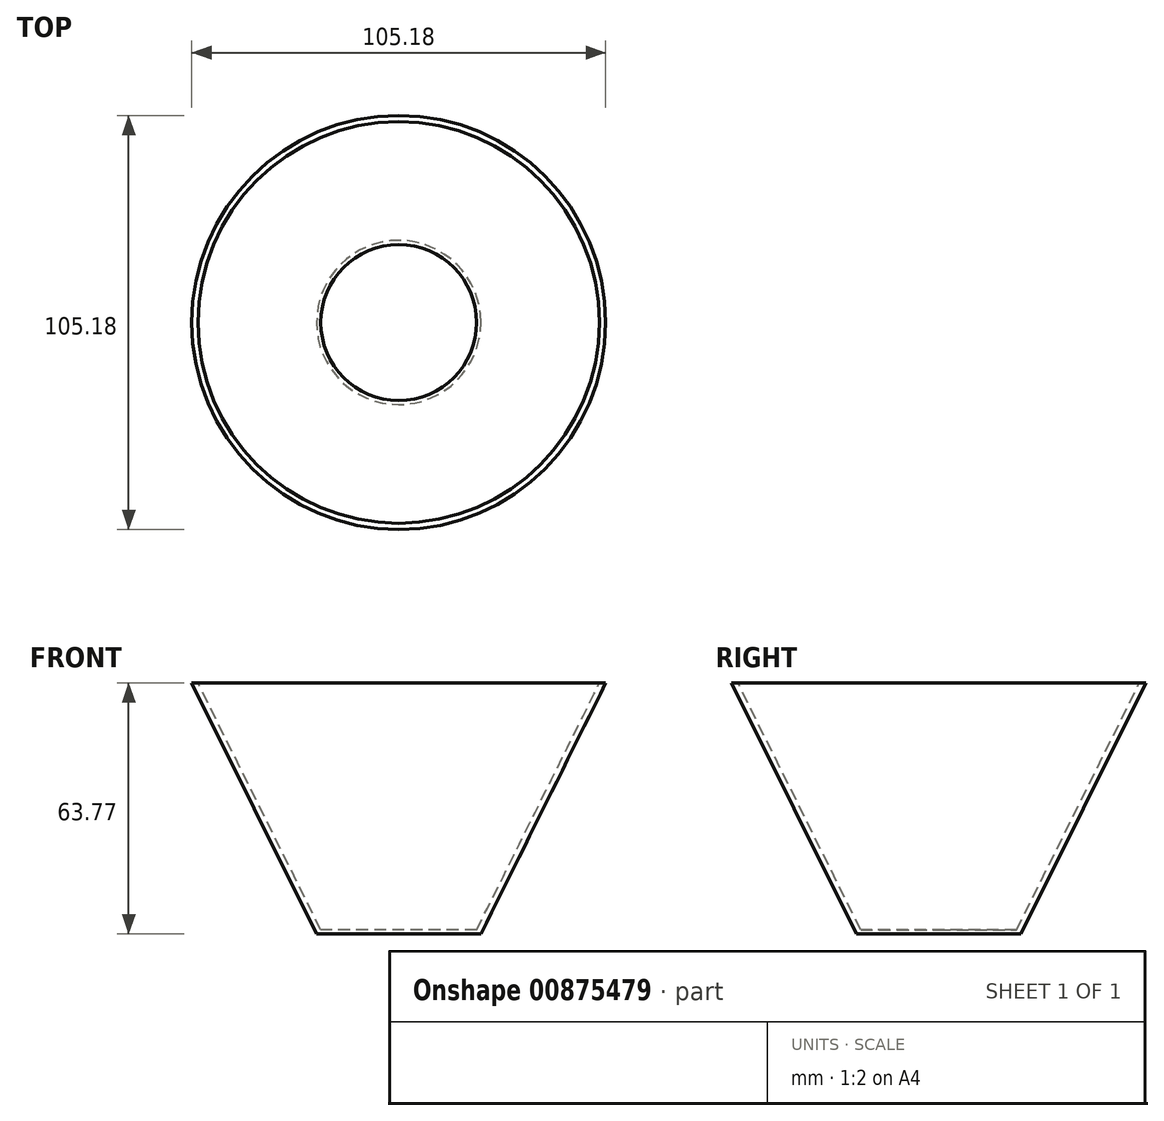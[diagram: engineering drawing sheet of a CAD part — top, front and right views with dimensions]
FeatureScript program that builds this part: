
annotation { "Feature Type Name" : "Feature", "Feature Type Description" : "" }
export const myFeature = defineFeature(function(context is Context, id is Id, definition is map)
    precondition{}
    {
        {
            var Q0;
            Q0=qCreatedBy(makeId("Front.planeOp"),FACE);
            var sketch = newSketch(context, id + "F0", { "sketchPlane" : qUnion([Q0])});
            skLineSegment(sketch, "E0", {"start": v(0, 0) * mm, "end": v(-20.86, 0) * mm});
            skLineSegment(sketch, "E1", {"start": v(-20.86, 0) * mm, "end": v(-52.59, 63.77) * mm});
            skLineSegment(sketch, "E2", {"start": v(-52.59, 63.77) * mm, "end": v(-51, 63.77) * mm});
            skLineSegment(sketch, "E3", {"start": v(0, 1.05) * mm, "end": v(0, 0) * mm});
            skLineSegment(sketch, "E4", {"start": v(-51, 63.77) * mm, "end": v(-19.8, 1.05) * mm});
            skLineSegment(sketch, "E5", {"start": v(-19.8, 1.05) * mm, "end": v(0, 1.05) * mm});
            skSolve(sketch);
        }
        {
            var Q0;
            Q0 = qSketchRegion(id + "F0", true);
            var Q1;
            Q1=makeQuery(id+"F0.imprint","IMPRINT",FACE,{"disambiguationData":[TD([[makeQuery(id+"F0.imprint","IMPRINT",EDGE,{"derivedFrom":sQuery(id+"F0.wireOp",EDGE,"E0")}),-1.0]])]});
            var Q2;
            Q2=sQuery(id+"F0.wireOp",EDGE,"E3");
            revolve(context, id + "F1", {"surfaceOperationType" : NewSurfaceOperationType.NEW, "entities" : qUnion([Q0, Q1]), "axis" : qUnion([Q2]), "revolveType" : RevolveType.FULL});
        }
    });
